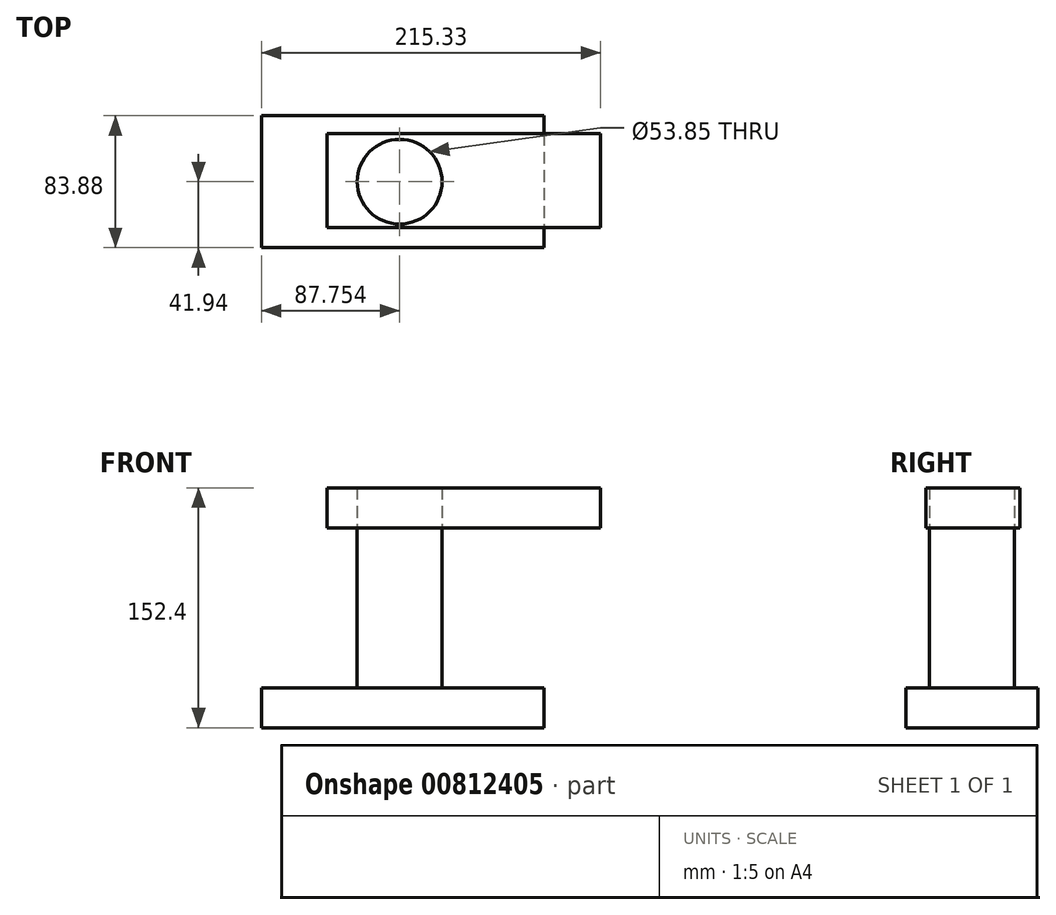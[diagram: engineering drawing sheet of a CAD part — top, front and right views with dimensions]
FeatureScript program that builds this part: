
annotation { "Feature Type Name" : "Feature", "Feature Type Description" : "" }
export const myFeature = defineFeature(function(context is Context, id is Id, definition is map)
    precondition{}
    {
        {
            var Q0;
            Q0=qCreatedBy(makeId("Top.planeOp"),FACE);
            var sketch = newSketch(context, id + "F0", { "sketchPlane" : qUnion([Q0])});
            skLineSegment(sketch, "E0.bottom", {"start": v(-89.69, 41.94) * mm, "end": v(89.69, 41.94) * mm});
            skLineSegment(sketch, "E0.top", {"start": v(-89.69, -41.94) * mm, "end": v(89.69, -41.94) * mm});
            skLineSegment(sketch, "E0.left", {"start": v(-89.69, 41.94) * mm, "end": v(-89.69, -41.94) * mm});
            skLineSegment(sketch, "E0.right", {"start": v(89.69, 41.94) * mm, "end": v(89.69, -41.94) * mm});
            skPoint(sketch, "E0.middle", {"position": v(0, 0) * mm});
            skSolve(sketch);
        }
        {
            var Q0;
            Q0=makeQuery(id+"F0.imprint","IMPRINT",FACE,{"disambiguationData":[TD([[makeQuery(id+"F0.imprint","IMPRINT",EDGE,{"derivedFrom":sQuery(id+"F0.wireOp",EDGE,"E0.bottom")}),-1.0]])]});
            extrude(context, id + "F1", {"entities" : qUnion([Q0]), "depth" : 25.4 * mm, "offsetDistance" : 25.4 * mm});
        }
        {
            var Q0;
            Q0=makeQuery(id+"F1.opExtrude","CAP_FACE",FACE,{"disambiguationData":[OSD([sQuery(id+"F0.wireOp",EDGE,"E0.bottom"),sQuery(id+"F0.wireOp",EDGE,"E0.top"),sQuery(id+"F0.wireOp",EDGE,"E0.left"),sQuery(id+"F0.wireOp",EDGE,"E0.right")])],"isStart":false});
            var sketch = newSketch(context, id + "F2", { "sketchPlane" : qUnion([Q0])});
            skCircle(sketch, "E1", {"center": v(-1.94, 0) * mm, "radius": 26.93 * mm});
            skSolve(sketch);
        }
        {
            var Q0;
            Q0=makeQuery(id+"F2.imprint","IMPRINT",FACE,{"disambiguationData":[TD([[makeQuery(id+"F2.imprint","IMPRINT",EDGE,{"derivedFrom":sQuery(id+"F2.wireOp",EDGE,"E1")}),1.0]])]});
            extrude(context, id + "F3", {"entities" : qUnion([Q0]), "depth" : 101.6 * mm, "offsetDistance" : 25.4 * mm});
        }
        {
            var Q0;
            Q0=makeQuery(id+"F3.opExtrude","CAP_FACE",FACE,{"disambiguationData":[OSD([sQuery(id+"F2.wireOp",EDGE,"E1")])],"isStart":false});
            var sketch = newSketch(context, id + "F4", { "sketchPlane" : qUnion([Q0])});
            skLineSegment(sketch, "E2.bottom", {"start": v(-48.02, 30.51) * mm, "end": v(125.64, 30.51) * mm});
            skLineSegment(sketch, "E2.top", {"start": v(-48.02, -29.04) * mm, "end": v(125.64, -29.04) * mm});
            skLineSegment(sketch, "E2.left", {"start": v(-48.02, 30.51) * mm, "end": v(-48.02, -29.04) * mm});
            skLineSegment(sketch, "E2.right", {"start": v(125.64, 30.51) * mm, "end": v(125.64, -29.04) * mm});
            skSolve(sketch);
        }
        {
            var Q0;
            Q0=makeQuery(id+"F4.imprint","IMPRINT",FACE,{"disambiguationData":[TD([[makeQuery(id+"F4.imprint","IMPRINT",EDGE,{"derivedFrom":sQuery(id+"F4.wireOp",EDGE,"E2.bottom")}),-1.0]])]});
            extrude(context, id + "F5", {"entities" : qUnion([Q0]), "depth" : 25.4 * mm, "offsetDistance" : 25.4 * mm});
        }
    });
